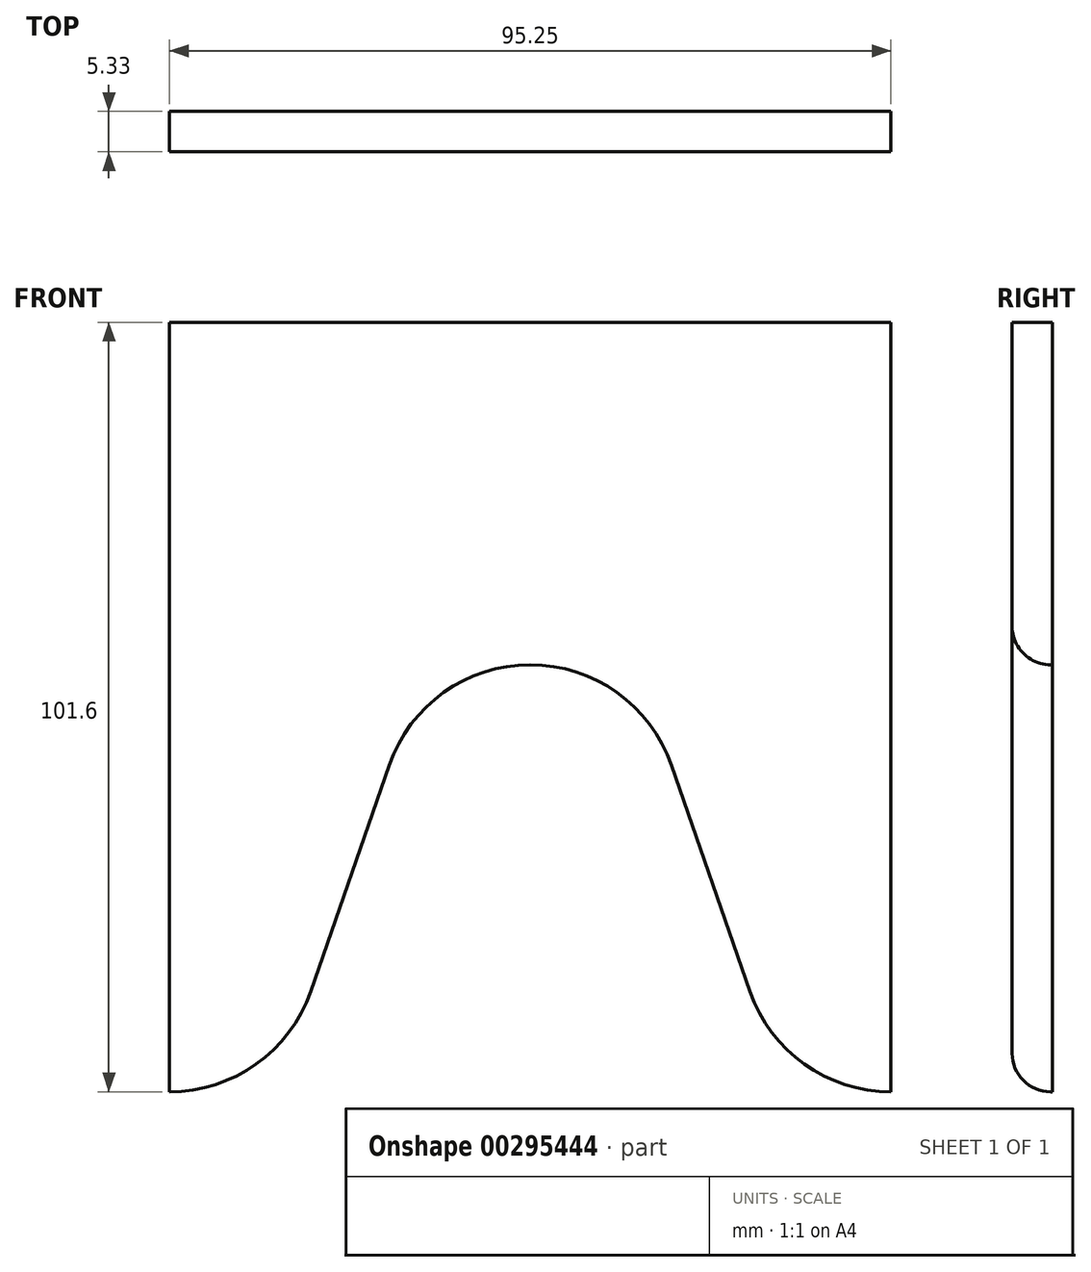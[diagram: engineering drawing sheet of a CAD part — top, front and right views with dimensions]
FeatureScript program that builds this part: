
annotation { "Feature Type Name" : "Feature", "Feature Type Description" : "" }
export const myFeature = defineFeature(function(context is Context, id is Id, definition is map)
    precondition{}
    {
        {
            var Q0;
            Q0=qCreatedBy(makeId("Front.planeOp"),FACE);
            var sketch = newSketch(context, id + "F0", { "sketchPlane" : qUnion([Q0])});
            skLineSegment(sketch, "E0.bottom", {"start": v(0, 0) * mm, "end": v(95.25, 0) * mm});
            skLineSegment(sketch, "E0.left", {"start": v(0, 0) * mm, "end": v(0, -101.6) * mm});
            skLineSegment(sketch, "E0.right", {"start": v(95.25, 0) * mm, "end": v(95.25, -101.6) * mm});
            skLineSegment(sketch, "E1", {"start": v(47.63, 0) * mm, "end": v(47.63, -138.97) * mm, "construction": true});
            skArc(sketch, "E2", {"start": v(66.25, -58.48) * mm, "mid": v(47.62, -45.23) * mm, "end": v(29, -58.48) * mm});
            skPoint(sketch, "E3", {"position": v(47.63, -69.49) * mm});
            skArc(sketch, "E4", {"start": v(0, -101.6) * mm, "mid": v(11.43, -97.95) * mm, "end": v(18.63, -88.35) * mm});
            skArc(sketch, "E5", {"start": v(76.62, -88.35) * mm, "mid": v(83.82, -97.95) * mm, "end": v(95.25, -101.6) * mm});
            skLineSegment(sketch, "E6", {"start": v(18.63, -88.35) * mm, "end": v(29, -58.48) * mm});
            skLineSegment(sketch, "E7", {"start": v(76.62, -88.35) * mm, "end": v(66.25, -58.48) * mm});
            skSolve(sketch);
        }
        {
            var Q0;
            Q0 = qSketchRegion(id + "F0", true);
            extrude(context, id + "F1", {"entities" : qUnion([Q0]), "depth" : 5.33 * mm});
        }
        {
            var Q0;
            Q0=makeQuery(id+"F1.opExtrude","CAP_EDGE",EDGE,{"disambiguationData":[OSD([sQuery(id+"F0.wireOp",EDGE,"E4")])],"isStart":false});
            fillet(context, id + "F2", {"entities" : qUnion([Q0]), "radius" : 5.08 * mm, "tangentPropagation" : true, "allowEdgeOverflow" : false});
        }
    });
